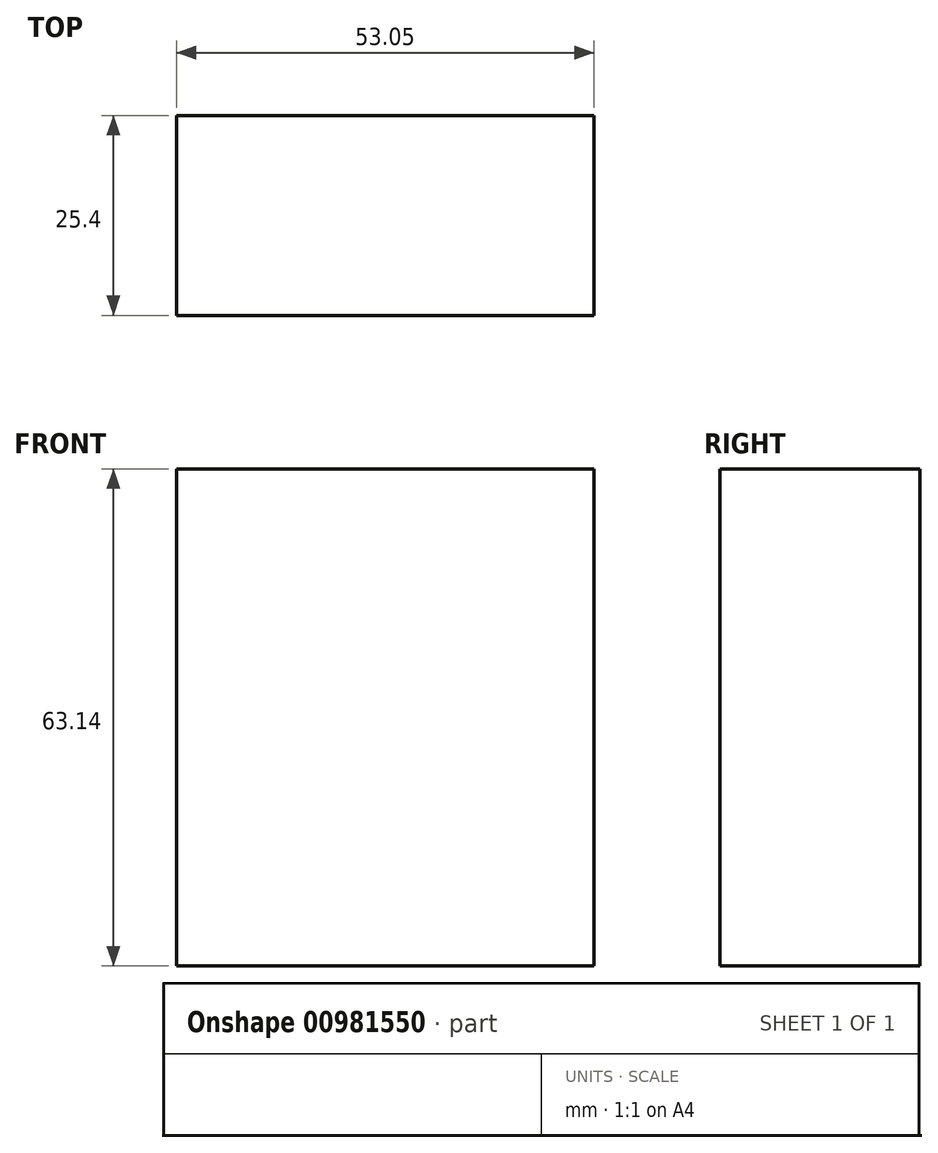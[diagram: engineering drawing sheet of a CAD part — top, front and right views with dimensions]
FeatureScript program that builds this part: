
annotation { "Feature Type Name" : "Feature", "Feature Type Description" : "" }
export const myFeature = defineFeature(function(context is Context, id is Id, definition is map)
    precondition{}
    {
        {
            var Q0;
            Q0=qCreatedBy(makeId("Front.planeOp"),FACE);
            var sketch = newSketch(context, id + "F0", { "sketchPlane" : qUnion([Q0])});
            skLineSegment(sketch, "E0.bottom", {"start": v(-53.05, 33.34) * mm, "end": v(0, 33.34) * mm});
            skLineSegment(sketch, "E0.top", {"start": v(-53.05, -29.8) * mm, "end": v(0, -29.8) * mm});
            skLineSegment(sketch, "E0.left", {"start": v(-53.05, 33.34) * mm, "end": v(-53.05, -29.8) * mm});
            skLineSegment(sketch, "E0.right", {"start": v(0, 33.34) * mm, "end": v(0, -29.8) * mm});
            skSolve(sketch);
        }
        {
            var Q0;
            Q0=makeQuery(id+"F0.imprint","IMPRINT",FACE,{"disambiguationData":[TD([[makeQuery(id+"F0.imprint","IMPRINT",EDGE,{"derivedFrom":sQuery(id+"F0.wireOp",EDGE,"E0.bottom")}),-1.0]])]});
            var sketch = newSketch(context, id + "F1", { "sketchPlane" : qUnion([Q0])});
            skSolve(sketch);
        }
        {
            var Q0;
            Q0=makeQuery(id+"F1.imprint","IMPRINT",FACE,{"disambiguationData":[TD([[makeQuery(id+"F1.imprint","IMPRINT",EDGE,{"derivedFrom":makeQuery(id+"F0.imprint","IMPRINT",EDGE,{"derivedFrom":sQuery(id+"F0.wireOp",EDGE,"E0.bottom")})}),-1.0]])]});
            extrude(context, id + "F2", {"entities" : qUnion([Q0]), "depth" : 25.4 * mm, "offsetDistance" : 25.4 * mm});
        }
    });
